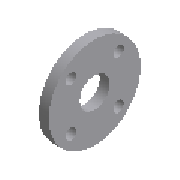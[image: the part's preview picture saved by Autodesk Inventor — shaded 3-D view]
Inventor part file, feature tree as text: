
AUTODESK INVENTOR PART (.ipt)
format: ipt  version: 2024.2 (Build 282272000, 272)  size: 184,320 bytes
history: native  units: mm (DEFAULTED — no unit token found)
features: other x6, revolve x1, extrude x1, pattern_circular x1
ambient origin geometry x8: Origin, YZ Plane, XZ Plane, XY Plane, X Axis, Y Axis, Z Axis, Center Point
bodies: Solid1 (feature_tree)
feature tree (9):
  other  "DIN EN 1092-1 Plate Flange for Welding Type 01 - PN 16 400 x 406.4"
  revolve  "Revolution1"  Angle=90.0deg
  extrude  "Extrusion1"  Depth=580.0mm
  pattern_circular  "Circular Pattern1"  [2 undecoded]
  other  "Work Axis1"
  other  "Work Point1"
  other  "Work Axis2"
  other  "Work Point2"
  other  "Work Point3"
note: 2 required parameter values undecoded (feature->parameter linkage not recoverable at this tier; creation-order binding heuristic only, values carry confidence <= 0.55)
